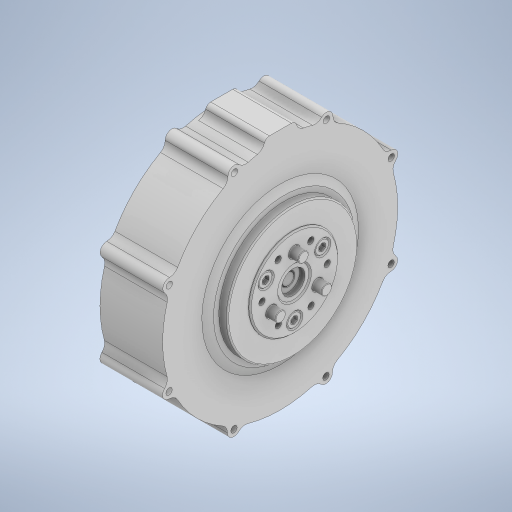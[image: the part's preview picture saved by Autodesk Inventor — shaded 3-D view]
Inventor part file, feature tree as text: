
AUTODESK INVENTOR PART (.ipt)
format: ipt  version: 2024.3 (Build 283343000, 343)  size: 1,035,264 bytes
history: native  units: mm
features: other x1, extrude x1, sketch x1
ambient origin geometry x8: Origin, YZ Plane, XZ Plane, XY Plane, X Axis, Y Axis, Z Axis, Center Point
bodies: 实体1 (feature_tree)
feature tree (3):
  other  "ソリッド1"
  extrude  "押し出し1"  Depth=3.0mm TaperAngle=0.0deg
  sketch  "スケッチ1"
